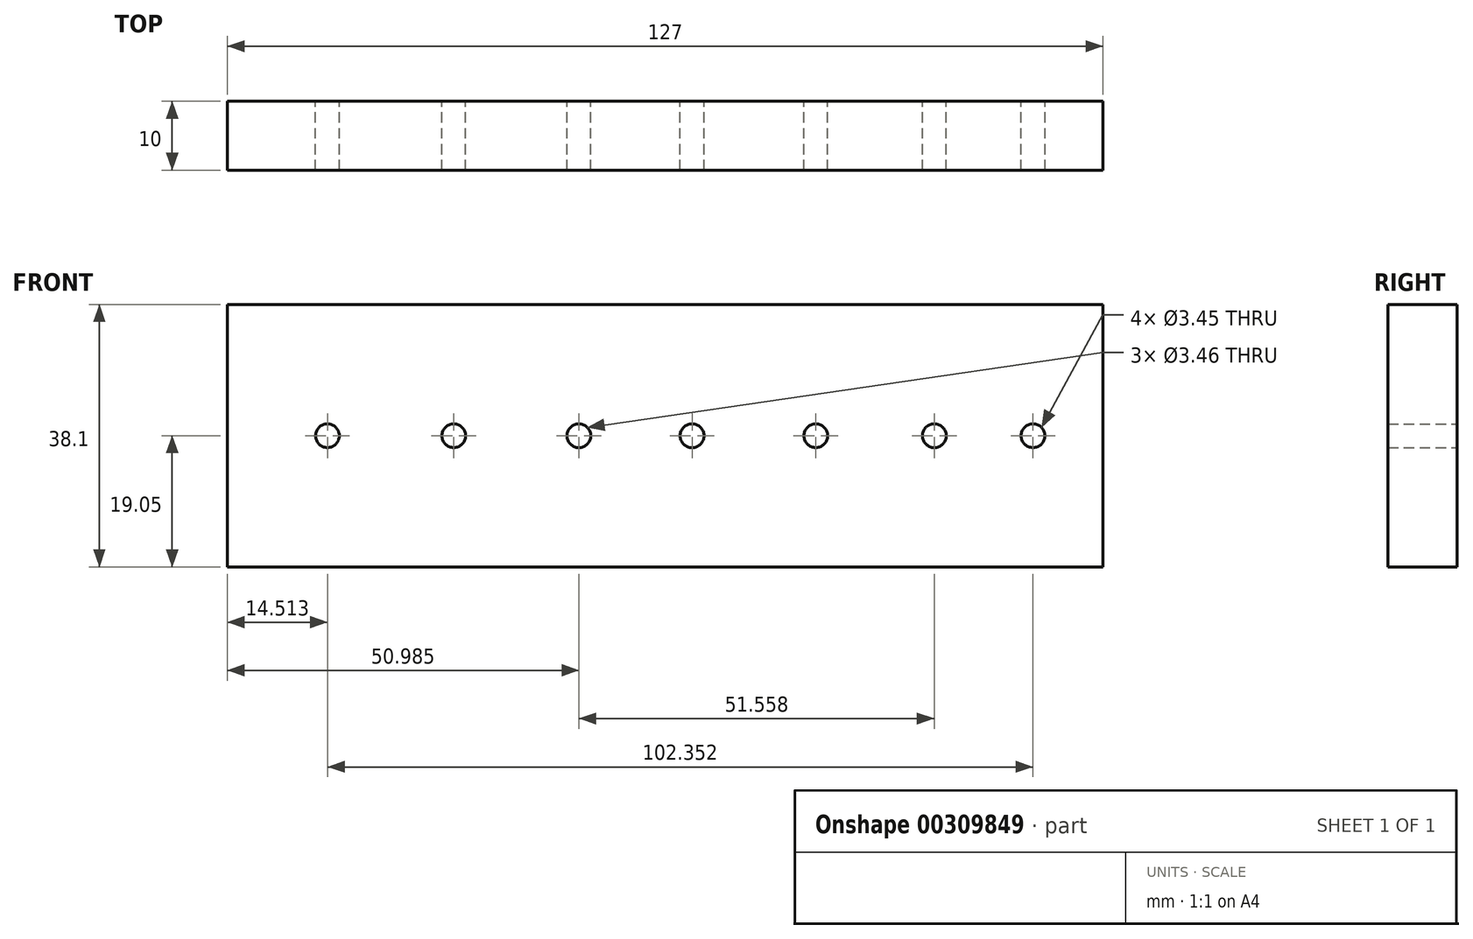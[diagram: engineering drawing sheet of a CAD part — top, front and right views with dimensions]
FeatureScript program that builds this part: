
annotation { "Feature Type Name" : "Feature", "Feature Type Description" : "" }
export const myFeature = defineFeature(function(context is Context, id is Id, definition is map)
    precondition{}
    {
        {
            var Q0;
            Q0=qCreatedBy(makeId("Front.planeOp"),FACE);
            var sketch = newSketch(context, id + "F0", { "sketchPlane" : qUnion([Q0])});
            skLineSegment(sketch, "E0.bottom", {"start": v(0, 0) * mm, "end": v(127, 0) * mm});
            skLineSegment(sketch, "E0.top", {"start": v(0, -38.1) * mm, "end": v(127, -38.1) * mm});
            skLineSegment(sketch, "E0.left", {"start": v(0, 0) * mm, "end": v(0, -38.1) * mm});
            skLineSegment(sketch, "E0.right", {"start": v(127, 0) * mm, "end": v(127, -38.1) * mm});
            skSolve(sketch);
        }
        {
            var Q0;
            Q0=makeQuery(id+"F0.imprint","IMPRINT",FACE,{"disambiguationData":[TD([[makeQuery(id+"F0.imprint","IMPRINT",EDGE,{"derivedFrom":sQuery(id+"F0.wireOp",EDGE,"E0.bottom")}),-1.0]])]});
            extrude(context, id + "F1", {"entities" : qUnion([Q0]), "depth" : 10 * mm});
        }
        {
            var Q0;
            Q0=qCreatedBy(makeId("Front.planeOp"),FACE);
            var sketch = newSketch(context, id + "F2", { "sketchPlane" : qUnion([Q0])});
            skPoint(sketch, "E1", {"position": v(0, 0) * mm});
            skPoint(sketch, "E2", {"position": v(0, -19.05) * mm});
            skPoint(sketch, "E3", {"position": v(14.51, -19.05) * mm});
            skPoint(sketch, "E4", {"position": v(32.84, -19.05) * mm});
            skPoint(sketch, "E5", {"position": v(85.36, -19.05) * mm});
            skPoint(sketch, "E6", {"position": v(116.86, -19.05) * mm});
            skPoint(sketch, "E7", {"position": v(102.54, -19.05) * mm});
            skPoint(sketch, "E8", {"position": v(50.98, -19.05) * mm});
            skPoint(sketch, "E9", {"position": v(67.4, -19.05) * mm});
            skSolve(sketch);
        }
        {
            var Q0;
            Q0=sQuery(id+"F2.wireOp",VERTEX,"E3");
            var Q1;
            Q1=makeQuery(id+"F1.opExtrude","SWEPT_BODY",BODY,{"disambiguationData":[OSD([sQuery(id+"F0.wireOp",EDGE,"E0.bottom"),sQuery(id+"F0.wireOp",EDGE,"E0.top"),sQuery(id+"F0.wireOp",EDGE,"E0.left"),sQuery(id+"F0.wireOp",EDGE,"E0.right")])]});
            hole(context, id + "F3", {"style" : HoleStyle.SIMPLE, "endStyle" : HoleEndStyle.THROUGH, "oppositeDirection" : true, "holeDiameter" : 3.45 * mm, "tappedDepth" : 12.7 * mm, "tapClearance" : 3, "locations" : qUnion([Q0]), "scope" : qUnion([Q1])});
        }
        {
            var Q0;
            Q0=sQuery(id+"F2.wireOp",VERTEX,"E4");
            var Q1;
            Q1=makeQuery(id+"F1.opExtrude","SWEPT_BODY",BODY,{"disambiguationData":[OSD([sQuery(id+"F0.wireOp",EDGE,"E0.bottom"),sQuery(id+"F0.wireOp",EDGE,"E0.top"),sQuery(id+"F0.wireOp",EDGE,"E0.left"),sQuery(id+"F0.wireOp",EDGE,"E0.right")])]});
            hole(context, id + "F4", {"style" : HoleStyle.SIMPLE, "endStyle" : HoleEndStyle.THROUGH, "oppositeDirection" : true, "holeDiameter" : 3.45 * mm, "tappedDepth" : 12.7 * mm, "tapClearance" : 3, "locations" : qUnion([Q0]), "scope" : qUnion([Q1])});
        }
        {
            var Q0;
            Q0=sQuery(id+"F2.wireOp",VERTEX,"E5");
            var Q1;
            Q1=makeQuery(id+"F1.opExtrude","SWEPT_BODY",BODY,{"disambiguationData":[OSD([sQuery(id+"F0.wireOp",EDGE,"E0.bottom"),sQuery(id+"F0.wireOp",EDGE,"E0.top"),sQuery(id+"F0.wireOp",EDGE,"E0.left"),sQuery(id+"F0.wireOp",EDGE,"E0.right")])]});
            hole(context, id + "F5", {"style" : HoleStyle.SIMPLE, "endStyle" : HoleEndStyle.THROUGH, "oppositeDirection" : true, "holeDiameter" : 3.45 * mm, "tappedDepth" : 12.7 * mm, "tapClearance" : 3, "locations" : qUnion([Q0]), "scope" : qUnion([Q1])});
        }
        {
            var Q0;
            Q0=sQuery(id+"F2.wireOp",VERTEX,"E6");
            var Q1;
            Q1=makeQuery(id+"F1.opExtrude","SWEPT_BODY",BODY,{"disambiguationData":[OSD([sQuery(id+"F0.wireOp",EDGE,"E0.bottom"),sQuery(id+"F0.wireOp",EDGE,"E0.top"),sQuery(id+"F0.wireOp",EDGE,"E0.left"),sQuery(id+"F0.wireOp",EDGE,"E0.right")])]});
            hole(context, id + "F6", {"style" : HoleStyle.SIMPLE, "endStyle" : HoleEndStyle.THROUGH, "oppositeDirection" : true, "holeDiameter" : 3.45 * mm, "tappedDepth" : 12.7 * mm, "tapClearance" : 3, "locations" : qUnion([Q0]), "scope" : qUnion([Q1])});
        }
        {
            var Q0;
            Q0=sQuery(id+"F2.wireOp",VERTEX,"E8");
            var Q1;
            Q1=makeQuery(id+"F1.opExtrude","SWEPT_BODY",BODY,{"disambiguationData":[OSD([sQuery(id+"F0.wireOp",EDGE,"E0.bottom"),sQuery(id+"F0.wireOp",EDGE,"E0.top"),sQuery(id+"F0.wireOp",EDGE,"E0.left"),sQuery(id+"F0.wireOp",EDGE,"E0.right")])]});
            hole(context, id + "F7", {"style" : HoleStyle.SIMPLE, "endStyle" : HoleEndStyle.THROUGH, "oppositeDirection" : true, "holeDiameter" : 3.46 * mm, "tappedDepth" : 12.7 * mm, "tapClearance" : 3, "locations" : qUnion([Q0]), "scope" : qUnion([Q1])});
        }
        {
            var Q0;
            Q0=sQuery(id+"F2.wireOp",VERTEX,"E9");
            var Q1;
            Q1=makeQuery(id+"F1.opExtrude","SWEPT_BODY",BODY,{"disambiguationData":[OSD([sQuery(id+"F0.wireOp",EDGE,"E0.bottom"),sQuery(id+"F0.wireOp",EDGE,"E0.top"),sQuery(id+"F0.wireOp",EDGE,"E0.left"),sQuery(id+"F0.wireOp",EDGE,"E0.right")])]});
            hole(context, id + "F8", {"style" : HoleStyle.SIMPLE, "endStyle" : HoleEndStyle.THROUGH, "oppositeDirection" : true, "holeDiameter" : 3.46 * mm, "tappedDepth" : 12.7 * mm, "tapClearance" : 3, "locations" : qUnion([Q0]), "scope" : qUnion([Q1])});
        }
        {
            var Q0;
            Q0=sQuery(id+"F2.wireOp",VERTEX,"E7");
            var Q1;
            Q1=makeQuery(id+"F1.opExtrude","SWEPT_BODY",BODY,{"disambiguationData":[OSD([sQuery(id+"F0.wireOp",EDGE,"E0.bottom"),sQuery(id+"F0.wireOp",EDGE,"E0.top"),sQuery(id+"F0.wireOp",EDGE,"E0.left"),sQuery(id+"F0.wireOp",EDGE,"E0.right")])]});
            hole(context, id + "F9", {"style" : HoleStyle.SIMPLE, "endStyle" : HoleEndStyle.THROUGH, "oppositeDirection" : true, "holeDiameter" : 3.46 * mm, "tappedDepth" : 12.7 * mm, "tapClearance" : 3, "locations" : qUnion([Q0]), "scope" : qUnion([Q1])});
        }
    });
